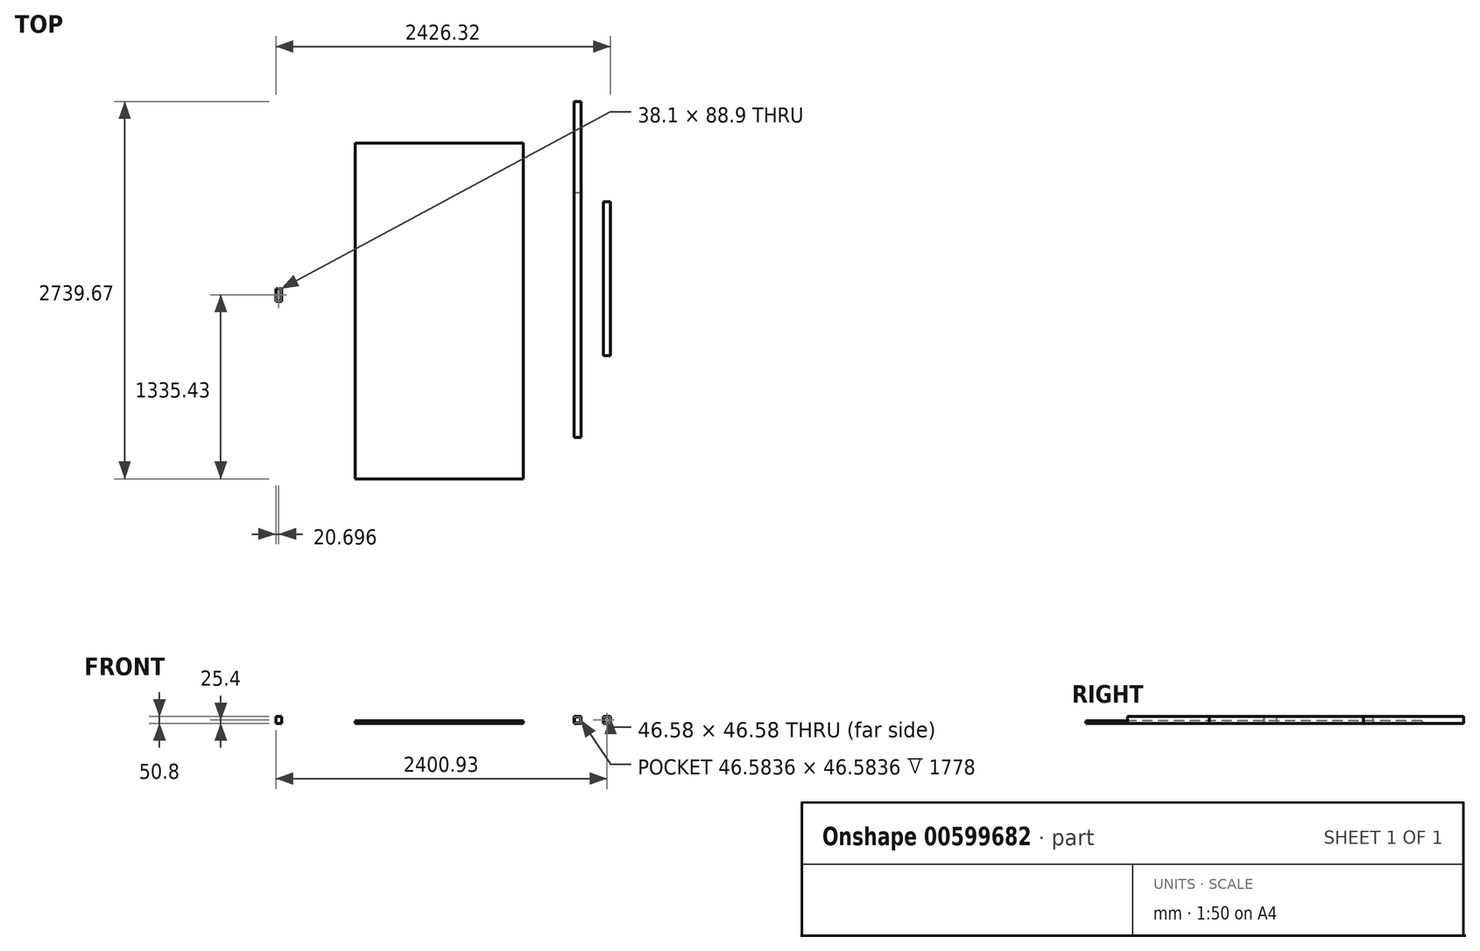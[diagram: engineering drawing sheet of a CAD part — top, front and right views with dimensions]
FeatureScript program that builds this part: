
annotation { "Feature Type Name" : "Feature", "Feature Type Description" : "" }
export const myFeature = defineFeature(function(context is Context, id is Id, definition is map)
    precondition{}
    {
        {
            var Q0;
            Q0=qCreatedBy(makeId("Top.planeOp"),FACE);
            var sketch = newSketch(context, id + "F0", { "sketchPlane" : qUnion([Q0])});
            skLineSegment(sketch, "E0.bottom", {"start": v(609.6, 1219.2) * mm, "end": v(-609.6, 1219.2) * mm});
            skLineSegment(sketch, "E0.top", {"start": v(609.6, -1219.2) * mm, "end": v(-609.6, -1219.2) * mm});
            skLineSegment(sketch, "E0.left", {"start": v(609.6, 1219.2) * mm, "end": v(609.6, -1219.2) * mm});
            skLineSegment(sketch, "E0.right", {"start": v(-609.6, 1219.2) * mm, "end": v(-609.6, -1219.2) * mm});
            skPoint(sketch, "E0.middle", {"position": v(0, 0) * mm});
            skSolve(sketch);
        }
        {
            var Q0;
            Q0=makeQuery(id+"F0.imprint","IMPRINT",FACE,{"disambiguationData":[TD([[makeQuery(id+"F0.imprint","IMPRINT",EDGE,{"derivedFrom":sQuery(id+"F0.wireOp",EDGE,"E0.bottom")}),1.0]])]});
            extrude(context, id + "F1", {"entities" : qUnion([Q0]), "depth" : 19.05 * mm, "offsetDistance" : 25.4 * mm});
        }
        {
            var Q0;
            Q0=qCreatedBy(makeId("Top.planeOp"),FACE);
            var sketch = newSketch(context, id + "F2", { "sketchPlane" : qUnion([Q0])});
            skLineSegment(sketch, "E1.bottom", {"start": v(-1183.96, 160.68) * mm, "end": v(-1145.86, 160.68) * mm});
            skLineSegment(sketch, "E1.top", {"start": v(-1183.96, 71.78) * mm, "end": v(-1145.86, 71.78) * mm});
            skLineSegment(sketch, "E1.left", {"start": v(-1183.96, 160.68) * mm, "end": v(-1183.96, 71.78) * mm});
            skLineSegment(sketch, "E1.right", {"start": v(-1145.86, 160.68) * mm, "end": v(-1145.86, 71.78) * mm});
            skLineSegment(sketch, "E2.bottom", {"start": v(-1144.21, 162.33) * mm, "end": v(-1185.61, 162.33) * mm});
            skLineSegment(sketch, "E2.top", {"start": v(-1144.21, 70.13) * mm, "end": v(-1185.61, 70.13) * mm});
            skLineSegment(sketch, "E2.left", {"start": v(-1144.21, 162.33) * mm, "end": v(-1144.21, 70.13) * mm});
            skLineSegment(sketch, "E2.right", {"start": v(-1185.61, 162.33) * mm, "end": v(-1185.61, 70.13) * mm});
            skPoint(sketch, "E2.middle", {"position": v(-1164.91, 116.23) * mm});
            skPoint(sketch, "E2.middle.positionSnap0", {"position": v(-1164.91, 160.68) * mm});
            skPoint(sketch, "E2.middle.positionSnap1", {"position": v(-1145.86, 116.23) * mm});
            skPoint(sketch, "E2.centerSnap0", {"position": v(-1164.91, 160.68) * mm});
            skPoint(sketch, "E2.centerSnap1", {"position": v(-1145.86, 116.23) * mm});
            skSolve(sketch);
        }
        {
            var Q0;
            Q0=makeQuery(id+"F2.imprint","IMPRINT",FACE,{"disambiguationData":[TD([[makeQuery(id+"F2.imprint","IMPRINT",EDGE,{"derivedFrom":sQuery(id+"F2.wireOp",EDGE,"E1.bottom")}),1.0]])]});
            extrude(context, id + "F3", {"entities" : qUnion([Q0]), "depth" : 50.8 * mm, "offsetDistance" : 25.4 * mm});
        }
        {
            var Q0;
            Q0=qCreatedBy(makeId("Top.planeOp"),FACE);
            var sketch = newSketch(context, id + "F4", { "sketchPlane" : qUnion([Q0])});
            skLineSegment(sketch, "E3.bottom", {"start": v(977.57, 1520.47) * mm, "end": v(1028.37, 1520.47) * mm});
            skLineSegment(sketch, "E3.top", {"start": v(977.57, -917.93) * mm, "end": v(1028.37, -917.93) * mm});
            skLineSegment(sketch, "E3.left", {"start": v(977.57, 1520.47) * mm, "end": v(977.57, -917.93) * mm});
            skLineSegment(sketch, "E3.right", {"start": v(1028.37, 1520.47) * mm, "end": v(1028.37, -917.93) * mm});
            skLineSegment(sketch, "E4.bottom", {"start": v(1189.91, 793.7) * mm, "end": v(1240.71, 793.7) * mm});
            skLineSegment(sketch, "E4.top", {"start": v(1189.91, -323.9) * mm, "end": v(1240.71, -323.9) * mm});
            skLineSegment(sketch, "E4.left", {"start": v(1189.91, 793.7) * mm, "end": v(1189.91, -323.9) * mm});
            skLineSegment(sketch, "E4.right", {"start": v(1240.71, 793.7) * mm, "end": v(1240.71, -323.9) * mm});
            skSolve(sketch);
        }
        {
            var Q0;
            Q0=makeQuery(id+"F4.imprint","IMPRINT",FACE,{"disambiguationData":[TD([[makeQuery(id+"F4.imprint","IMPRINT",EDGE,{"derivedFrom":sQuery(id+"F4.wireOp",EDGE,"E3.bottom")}),-1.0]])]});
            var Q1;
            Q1=makeQuery(id+"F4.imprint","IMPRINT",FACE,{"disambiguationData":[TD([[makeQuery(id+"F4.imprint","IMPRINT",EDGE,{"derivedFrom":sQuery(id+"F4.wireOp",EDGE,"E4.bottom")}),-1.0]])]});
            extrude(context, id + "F5", {"entities" : qUnion([Q0, Q1]), "depth" : 50.8 * mm, "offsetDistance" : 25.4 * mm});
        }
        {
            var Q0;
            Q0=makeQuery(id+"F5.opExtrude","SWEPT_FACE",FACE,{"disambiguationData":[OSD([sQuery(id+"F4.wireOp",EDGE,"E3.top")])]});
            var sketch = newSketch(context, id + "F6", { "sketchPlane" : qUnion([Q0])});
            skLineSegment(sketch, "E5.bottom", {"start": v(979.68, 48.7) * mm, "end": v(1026.26, 48.7) * mm});
            skLineSegment(sketch, "E5.top", {"start": v(979.68, 2.1) * mm, "end": v(1026.26, 2.1) * mm});
            skLineSegment(sketch, "E5.left", {"start": v(979.68, 48.7) * mm, "end": v(979.68, 2.1) * mm});
            skLineSegment(sketch, "E5.right", {"start": v(1026.26, 48.7) * mm, "end": v(1026.26, 2.1) * mm});
            skLineSegment(sketch, "E6", {"start": v(979.68, 2.1) * mm, "end": v(979.68, 0) * mm, "construction": true});
            skLineSegment(sketch, "E7", {"start": v(979.68, 0) * mm, "end": v(979.68, 2.1) * mm, "construction": true});
            skLineSegment(sketch, "E8", {"start": v(977.57, 2.1) * mm, "end": v(979.68, 2.1) * mm, "construction": true});
            skLineSegment(sketch, "E9", {"start": v(1026.26, 48.7) * mm, "end": v(1028.37, 48.7) * mm, "construction": true});
            skLineSegment(sketch, "E10", {"start": v(1028.37, 48.7) * mm, "end": v(1026.26, 48.7) * mm, "construction": true});
            skLineSegment(sketch, "E11", {"start": v(1026.26, 48.7) * mm, "end": v(1026.26, 50.8) * mm, "construction": true});
            skSolve(sketch);
        }
        {
            var Q0;
            Q0=makeQuery(id+"F6.imprint","IMPRINT",FACE,{"disambiguationData":[TD([[makeQuery(id+"F6.imprint","IMPRINT",EDGE,{"derivedFrom":sQuery(id+"F6.wireOp",EDGE,"E5.bottom")}),-1.0]])]});
            extrude(context, id + "F7", {"entities" : qUnion([Q0]), "operationType" : NewBodyOperationType.REMOVE, "oppositeDirection" : true, "depth" : 1778 * mm, "offsetDistance" : 25.4 * mm});
        }
        {
            var Q0;
            Q0=makeQuery(id+"F5.opExtrude","SWEPT_FACE",FACE,{"disambiguationData":[OSD([sQuery(id+"F4.wireOp",EDGE,"E4.top")])]});
            var sketch = newSketch(context, id + "F8", { "sketchPlane" : qUnion([Q0])});
            skLineSegment(sketch, "E12.bottom", {"start": v(1192.02, 48.7) * mm, "end": v(1238.6, 48.7) * mm});
            skLineSegment(sketch, "E12.top", {"start": v(1192.02, 2.1) * mm, "end": v(1238.6, 2.1) * mm});
            skLineSegment(sketch, "E12.left", {"start": v(1192.02, 48.7) * mm, "end": v(1192.02, 2.1) * mm});
            skLineSegment(sketch, "E12.right", {"start": v(1238.6, 48.7) * mm, "end": v(1238.6, 2.1) * mm});
            skLineSegment(sketch, "E13", {"start": v(1192.02, 2.1) * mm, "end": v(1192.02, 0) * mm, "construction": true});
            skLineSegment(sketch, "E14", {"start": v(1192.02, 2.1) * mm, "end": v(1189.91, 2.1) * mm, "construction": true});
            skLineSegment(sketch, "E15", {"start": v(1238.6, 48.7) * mm, "end": v(1240.71, 48.7) * mm, "construction": true});
            skLineSegment(sketch, "E16", {"start": v(1238.6, 48.7) * mm, "end": v(1238.6, 50.8) * mm, "construction": true});
            skSolve(sketch);
        }
        {
            var Q0;
            Q0=makeQuery(id+"F8.imprint","IMPRINT",FACE,{"disambiguationData":[TD([[makeQuery(id+"F8.imprint","IMPRINT",EDGE,{"derivedFrom":sQuery(id+"F8.wireOp",EDGE,"E12.bottom")}),-1.0]])]});
            extrude(context, id + "F9", {"entities" : qUnion([Q0]), "operationType" : NewBodyOperationType.REMOVE, "oppositeDirection" : true, "depth" : 1244.6 * mm, "offsetDistance" : 25.4 * mm});
        }
    });
